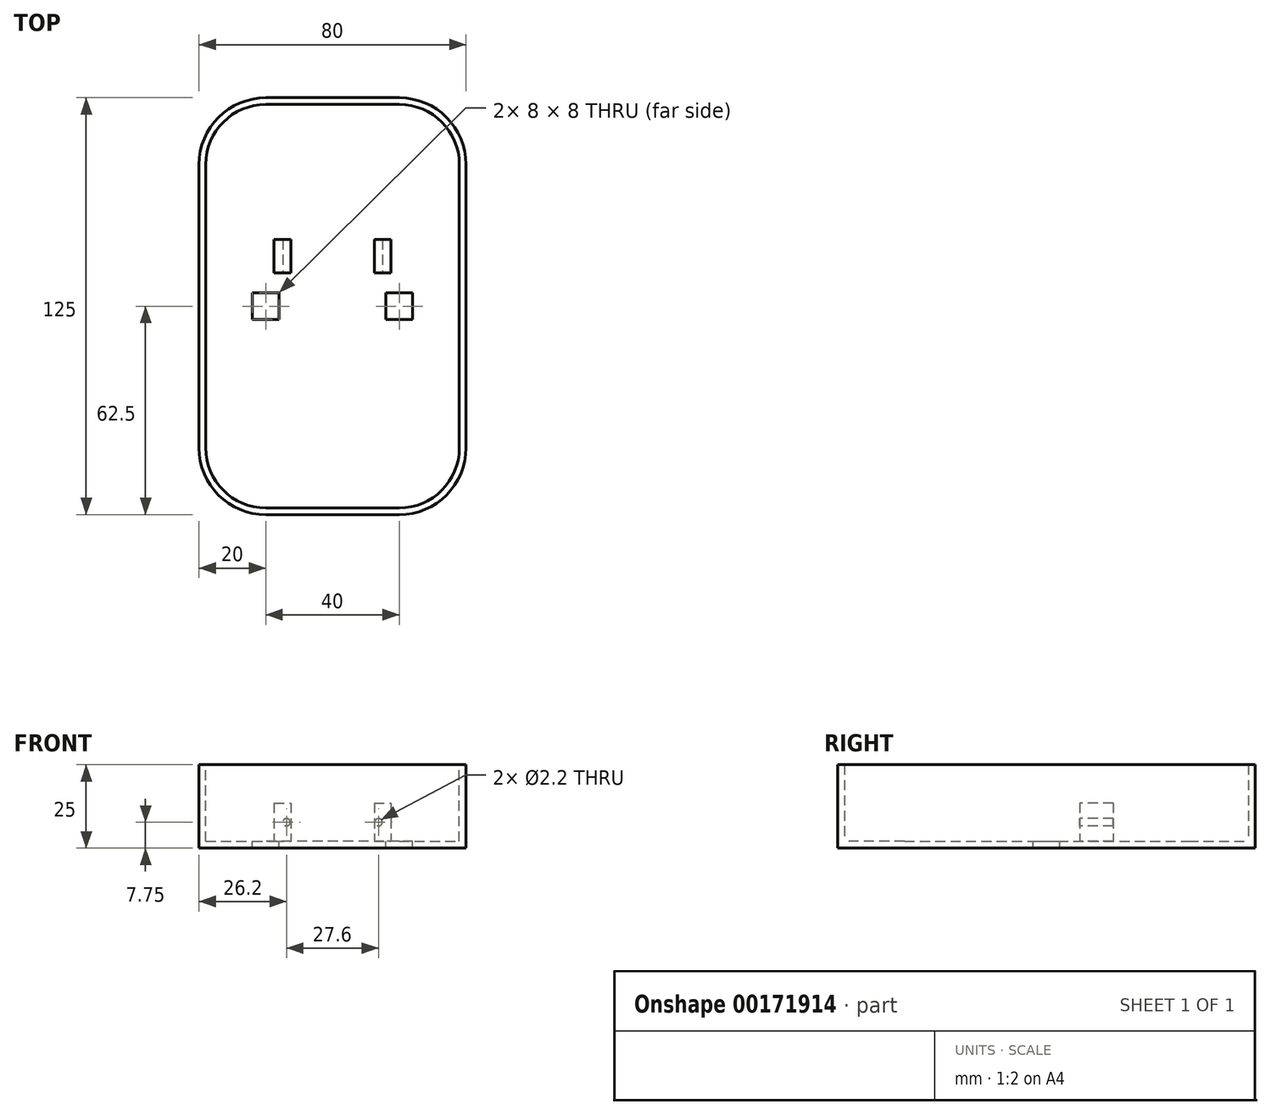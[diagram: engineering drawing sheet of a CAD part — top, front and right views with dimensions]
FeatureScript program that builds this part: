
annotation { "Feature Type Name" : "Feature", "Feature Type Description" : "" }
export const myFeature = defineFeature(function(context is Context, id is Id, definition is map)
    precondition{}
    {
        {
            var Q0;
            Q0=qCreatedBy(makeId("Top.planeOp"),FACE);
            var sketch = newSketch(context, id + "F0", { "sketchPlane" : qUnion([Q0])});
            skLineSegment(sketch, "E0.bottom", {"start": v(20, -62.5) * mm, "end": v(-20, -62.5) * mm});
            skLineSegment(sketch, "E0.top", {"start": v(20, 62.5) * mm, "end": v(-20, 62.5) * mm});
            skLineSegment(sketch, "E0.left", {"start": v(40, -42.5) * mm, "end": v(40, 42.5) * mm});
            skLineSegment(sketch, "E0.right", {"start": v(-40, -42.5) * mm, "end": v(-40, 42.5) * mm});
            skPoint(sketch, "E0.middle", {"position": v(0, 0) * mm});
            skPoint(sketch, "E1.visualSharp", {"position": v(-40, 62.5) * mm});
            skArc(sketch, "E1.filletArc", {"start": v(-20, 62.5) * mm, "mid": v(-34.14, 56.64) * mm, "end": v(-40, 42.5) * mm});
            skPoint(sketch, "E2.visualSharp", {"position": v(-40, -62.5) * mm});
            skArc(sketch, "E2.filletArc", {"start": v(-40, -42.5) * mm, "mid": v(-34.14, -56.64) * mm, "end": v(-20, -62.5) * mm});
            skPoint(sketch, "E3.visualSharp", {"position": v(40, -62.5) * mm});
            skArc(sketch, "E3.filletArc", {"start": v(20, -62.5) * mm, "mid": v(34.14, -56.64) * mm, "end": v(40, -42.5) * mm});
            skPoint(sketch, "E4.visualSharp", {"position": v(40, 62.5) * mm});
            skArc(sketch, "E4.filletArc", {"start": v(40, 42.5) * mm, "mid": v(34.14, 56.64) * mm, "end": v(20, 62.5) * mm});
            skPoint(sketch, "E5.visualSharp", {"position": v(-38, -60.5) * mm});
            skPoint(sketch, "E6.visualSharp", {"position": v(38, -60.5) * mm});
            skPoint(sketch, "E7.visualSharp", {"position": v(38, 60.5) * mm});
            skPoint(sketch, "E8.visualSharp", {"position": v(-38, 60.5) * mm});
            skSolve(sketch);
        }
        {
            var Q0;
            Q0 = qSketchRegion(id + "F0", true);
            var Q1;
            Q1=makeQuery(id+"F0.imprint","IMPRINT",FACE,{"disambiguationData":[TD([[makeQuery(id+"F0.imprint","IMPRINT",EDGE,{"derivedFrom":sQuery(id+"F0.wireOp",EDGE,"bf44d477-7505-4df8-a0bd-4dc320236a31.0")}),-1.0]])]});
            extrude(context, id + "F1", {"entities" : qUnion([Q0, Q1]), "depth" : 2 * mm});
        }
        {
            var Q0;
            Q0=makeQuery(id+"F0.imprint","IMPRINT",FACE,{"disambiguationData":[TD([[makeQuery(id+"F0.imprint","IMPRINT",EDGE,{"derivedFrom":sQuery(id+"F0.wireOp",EDGE,"E0.bottom")}),-1.0]])]});
            extrude(context, id + "F2", {"entities" : qUnion([Q0]), "operationType" : NewBodyOperationType.ADD, "depth" : 25 * mm});
        }
        {
            var Q0;
            Q0=makeQuery(id+"F2.opExtrude","CAP_FACE",FACE,{"disambiguationData":[OSD([sQuery(id+"F0.wireOp",EDGE,"E0.bottom"),sQuery(id+"F0.wireOp",EDGE,"E0.top"),sQuery(id+"F0.wireOp",EDGE,"E0.left"),sQuery(id+"F0.wireOp",EDGE,"E0.right"),sQuery(id+"F0.wireOp",EDGE,"E1.filletArc"),sQuery(id+"F0.wireOp",EDGE,"E2.filletArc"),sQuery(id+"F0.wireOp",EDGE,"E3.filletArc"),sQuery(id+"F0.wireOp",EDGE,"E4.filletArc")])],"isStart":false});
            shell(context, id + "F3", {"entities" : qUnion([Q0]), "thickness" : 2 * mm});
        }
        {
            var Q0;
            Q0=makeQuery(id+"F3.opShell","OFFSET_FACE",FACE,{"disambiguationData":[OSD([sQuery(id+"F0.wireOp",EDGE,"E0.bottom"),sQuery(id+"F0.wireOp",EDGE,"E0.top"),sQuery(id+"F0.wireOp",EDGE,"E0.left"),sQuery(id+"F0.wireOp",EDGE,"E0.right"),sQuery(id+"F0.wireOp",EDGE,"E1.filletArc"),sQuery(id+"F0.wireOp",EDGE,"E2.filletArc"),sQuery(id+"F0.wireOp",EDGE,"E3.filletArc"),sQuery(id+"F0.wireOp",EDGE,"E4.filletArc")])]});
            var sketch = newSketch(context, id + "F4", { "sketchPlane" : qUnion([Q0])});
            skLineSegment(sketch, "E9.bottom", {"start": v(24, -4) * mm, "end": v(16, -4) * mm});
            skLineSegment(sketch, "E9.top", {"start": v(24, 4) * mm, "end": v(16, 4) * mm});
            skLineSegment(sketch, "E9.left", {"start": v(24, -4) * mm, "end": v(24, 4) * mm});
            skLineSegment(sketch, "E9.right", {"start": v(16, -4) * mm, "end": v(16, 4) * mm});
            skPoint(sketch, "E9.middle", {"position": v(20, 0) * mm});
            skLineSegment(sketch, "E10.MirrorCS", {"start": v(-16, -4) * mm, "end": v(-16, 4) * mm});
            skLineSegment(sketch, "E11.MirrorCS", {"start": v(-24, -4) * mm, "end": v(-16, -4) * mm});
            skLineSegment(sketch, "E12.MirrorCS", {"start": v(-24, -4) * mm, "end": v(-24, 4) * mm});
            skLineSegment(sketch, "E13.MirrorCS", {"start": v(-24, 4) * mm, "end": v(-16, 4) * mm});
            skSolve(sketch);
        }
        {
            var Q0;
            Q0 = qSketchRegion(id + "F4", true);
            extrude(context, id + "F5", {"entities" : qUnion([Q0]), "operationType" : NewBodyOperationType.REMOVE, "oppositeDirection" : true, "depth" : 25 * mm});
        }
        {
            var Q0;
            Q0=qCreatedBy(makeId("Front.planeOp"),FACE);
            var sketch = newSketch(context, id + "F6", { "sketchPlane" : qUnion([Q0])});
            skLineSegment(sketch, "E14.bottom", {"start": v(-17.5, 13.5) * mm, "end": v(17.5, 13.5) * mm});
            skLineSegment(sketch, "E14.top", {"start": v(-17.5, 2) * mm, "end": v(17.5, 2) * mm});
            skLineSegment(sketch, "E14.left", {"start": v(-17.5, 13.5) * mm, "end": v(-17.5, 2) * mm});
            skLineSegment(sketch, "E14.right", {"start": v(17.5, 13.5) * mm, "end": v(17.5, 2) * mm});
            skCircle(sketch, "E15", {"center": v(-13.8, 7.75) * mm, "radius": 1.1 * mm});
            skCircle(sketch, "E16", {"center": v(13.8, 7.75) * mm, "radius": 1.1 * mm});
            skSolve(sketch);
        }
        {
            var Q0;
            Q0=makeQuery(id+"F6.imprint","IMPRINT",FACE,{"disambiguationData":[TD([[makeQuery(id+"F6.imprint","IMPRINT",EDGE,{"derivedFrom":sQuery(id+"F6.wireOp",EDGE,"E14.bottom")}),-1.0]])]});
            extrude(context, id + "F7", {"entities" : qUnion([Q0]), "operationType" : NewBodyOperationType.ADD, "oppositeDirection" : true, "depth" : 30 * mm});
        }
        {
            var Q0;
            Q0=makeQuery(id+"F7.opExtrude","CAP_FACE",FACE,{"disambiguationData":[OSD([sQuery(id+"F6.wireOp",EDGE,"E14.bottom"),sQuery(id+"F6.wireOp",EDGE,"E14.top"),sQuery(id+"F6.wireOp",EDGE,"E14.left"),sQuery(id+"F6.wireOp",EDGE,"E14.right"),sQuery(id+"F6.wireOp",EDGE,"E15"),sQuery(id+"F6.wireOp",EDGE,"E16")])],"isStart":true});
            extrude(context, id + "F8", {"entities" : qUnion([Q0]), "operationType" : NewBodyOperationType.REMOVE, "oppositeDirection" : true, "depth" : 10 * mm});
        }
        {
            var Q0;
            Q0=makeQuery(id+"F8.boolean.opBoolean","COPY",FACE,{"derivedFrom":makeQuery(id+"F8.opExtrude","CAP_FACE",FACE,{"disambiguationData":[OSD([sQuery(id+"F6.wireOp",EDGE,"E14.bottom"),sQuery(id+"F6.wireOp",EDGE,"E14.top"),sQuery(id+"F6.wireOp",EDGE,"E14.left"),sQuery(id+"F6.wireOp",EDGE,"E14.right"),sQuery(id+"F6.wireOp",EDGE,"E15"),sQuery(id+"F6.wireOp",EDGE,"E16")])],"isStart":false})});
            var sketch = newSketch(context, id + "F9", { "sketchPlane" : qUnion([Q0])});
            skLineSegment(sketch, "E17.bottom", {"start": v(-12.5, 13.5) * mm, "end": v(12.5, 13.5) * mm});
            skLineSegment(sketch, "E17.top", {"start": v(-12.5, 2) * mm, "end": v(12.5, 2) * mm});
            skLineSegment(sketch, "E17.left", {"start": v(-12.5, 13.5) * mm, "end": v(-12.5, 2) * mm});
            skLineSegment(sketch, "E17.right", {"start": v(12.5, 13.5) * mm, "end": v(12.5, 2) * mm});
            skPoint(sketch, "E17.middle", {"position": v(0, 7.75) * mm});
            skPoint(sketch, "E17.middle.positionSnap0", {"position": v(-17.5, 7.75) * mm});
            skPoint(sketch, "E17.centerSnap0", {"position": v(-17.5, 7.75) * mm});
            skSolve(sketch);
        }
        {
            var Q0;
            Q0 = qSketchRegion(id + "F9", true);
            extrude(context, id + "F10", {"entities" : qUnion([Q0]), "operationType" : NewBodyOperationType.REMOVE, "oppositeDirection" : true, "depth" : 25 * mm});
        }
        {
            var Q0;
            {var subQ0=sQuery(id+"F6.wireOp",EDGE,"E16");var subQ1=sQuery(id+"F6.wireOp",EDGE,"E14.right");var subQ2=sQuery(id+"F6.wireOp",EDGE,"E14.bottom");var subQ3=sQuery(id+"F6.wireOp",EDGE,"E14.top");Q0=makeQuery(id+"F10.boolean.opBoolean","SPLIT",FACE,{"disambiguationData":[TD([makeQuery(id+"F7.opExtrude","SWEPT_FACE",FACE,{"disambiguationData":[OSD([subQ1])]})])],"derivedFrom":makeQuery(id+"F7.opExtrude","CAP_FACE",FACE,{"disambiguationData":[OSD([subQ2,subQ3,sQuery(id+"F6.wireOp",EDGE,"E14.left"),subQ1,sQuery(id+"F6.wireOp",EDGE,"E15"),subQ0])],"isStart":false})});}
            var Q1;
            {var subQ0=sQuery(id+"F6.wireOp",EDGE,"E15");var subQ1=sQuery(id+"F6.wireOp",EDGE,"E14.left");var subQ2=sQuery(id+"F6.wireOp",EDGE,"E14.top");var subQ3=sQuery(id+"F6.wireOp",EDGE,"E14.bottom");Q1=makeQuery(id+"F10.boolean.opBoolean","SPLIT",FACE,{"disambiguationData":[TD([makeQuery(id+"F7.opExtrude","SWEPT_FACE",FACE,{"disambiguationData":[OSD([subQ1])]})])],"derivedFrom":makeQuery(id+"F7.opExtrude","CAP_FACE",FACE,{"disambiguationData":[OSD([subQ3,subQ2,subQ1,sQuery(id+"F6.wireOp",EDGE,"E14.right"),subQ0,sQuery(id+"F6.wireOp",EDGE,"E16")])],"isStart":false})});}
            extrude(context, id + "F11", {"entities" : qUnion([Q0, Q1]), "operationType" : NewBodyOperationType.REMOVE, "oppositeDirection" : true, "depth" : 10 * mm});
        }
    });
